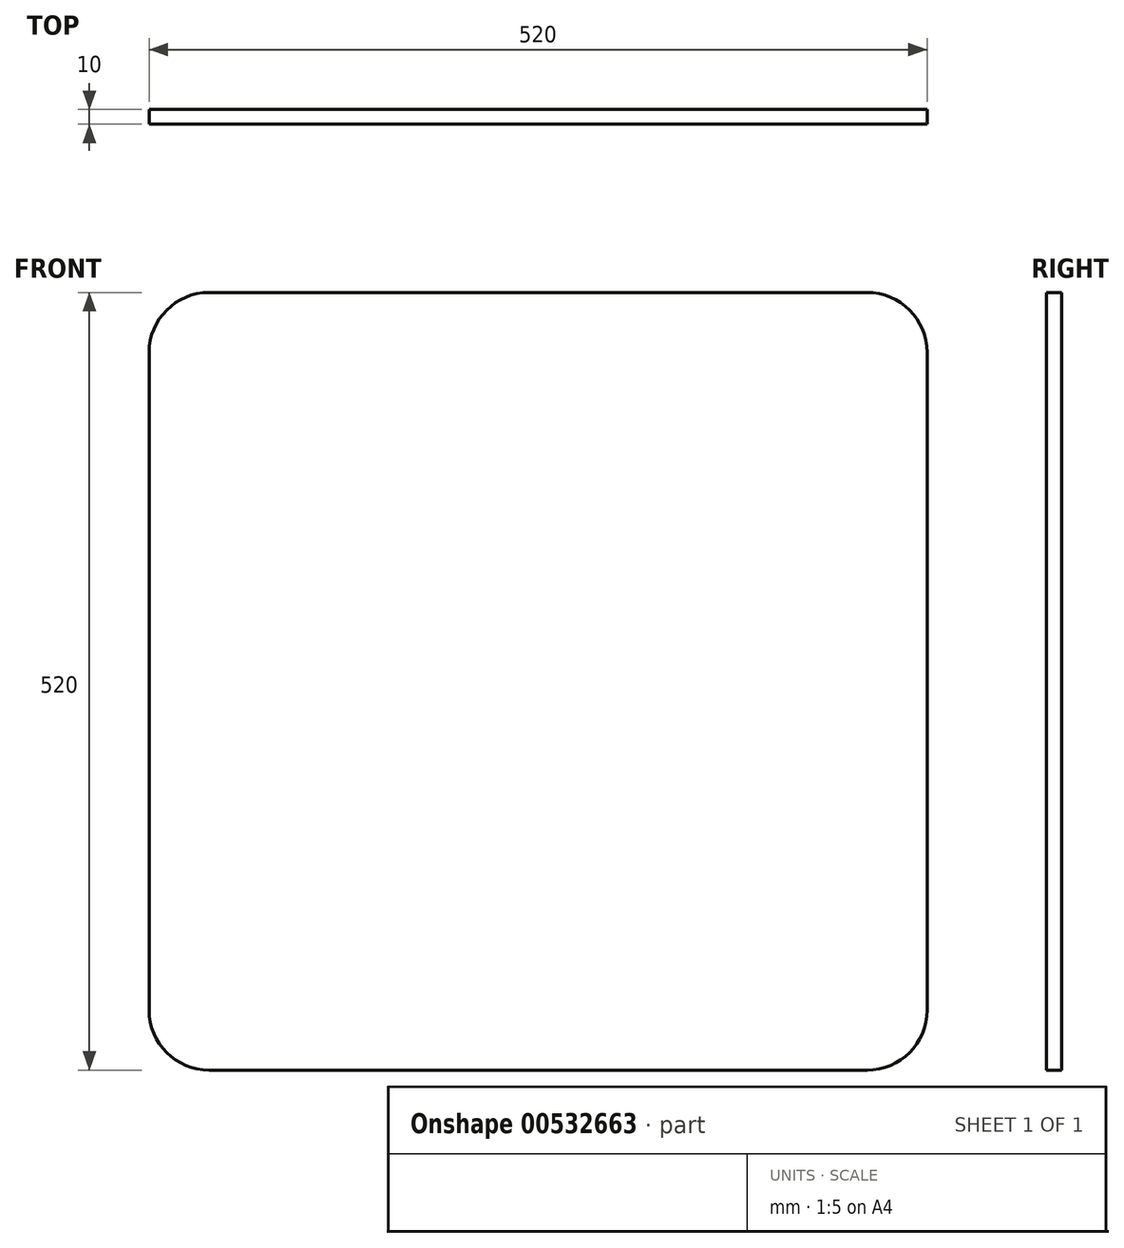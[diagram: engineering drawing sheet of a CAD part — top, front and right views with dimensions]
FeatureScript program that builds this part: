
annotation { "Feature Type Name" : "Feature", "Feature Type Description" : "" }
export const myFeature = defineFeature(function(context is Context, id is Id, definition is map)
    precondition{}
    {
        {
            var Q0;
            Q0=qCreatedBy(makeId("Front.planeOp"),FACE);
            var sketch = newSketch(context, id + "F0", { "sketchPlane" : qUnion([Q0])});
            skPoint(sketch, "E0.middle", {"position": v(0, 8.4) * mm});
            skArc(sketch, "E1.0", {"start": v(-215, 268.4) * mm, "mid": v(-243.28, 256.7) * mm, "end": v(-255, 228.4) * mm});
            skLineSegment(sketch, "E1.1", {"start": v(-215, 268.4) * mm, "end": v(225, 268.4) * mm});
            skLineSegment(sketch, "E1.2", {"start": v(-255, 228.4) * mm, "end": v(-255, -211.6) * mm});
            skArc(sketch, "E1.3", {"start": v(265, 228.4) * mm, "mid": v(253.28, 256.7) * mm, "end": v(225, 268.4) * mm});
            skArc(sketch, "E1.4", {"start": v(-255, -211.6) * mm, "mid": v(-243.28, -239.88) * mm, "end": v(-215, -251.6) * mm});
            skLineSegment(sketch, "E1.5", {"start": v(-215, -251.6) * mm, "end": v(225, -251.6) * mm});
            skArc(sketch, "E1.6", {"start": v(225, -251.6) * mm, "mid": v(253.28, -239.88) * mm, "end": v(265, -211.6) * mm});
            skLineSegment(sketch, "E1.7", {"start": v(265, 228.4) * mm, "end": v(265, -211.6) * mm});
            skSolve(sketch);
        }
        {
            var Q0;
            Q0=makeQuery(id+"F0.imprint","IMPRINT",FACE,{"disambiguationData":[TD([[makeQuery(id+"F0.imprint","IMPRINT",EDGE,{"derivedFrom":sQuery(id+"F0.wireOp",EDGE,"E1.0")}),1.0]])]});
            extrude(context, id + "F1", {"entities" : qUnion([Q0]), "depth" : 10 * mm, "offsetDistance" : 25 * mm});
        }
    });
